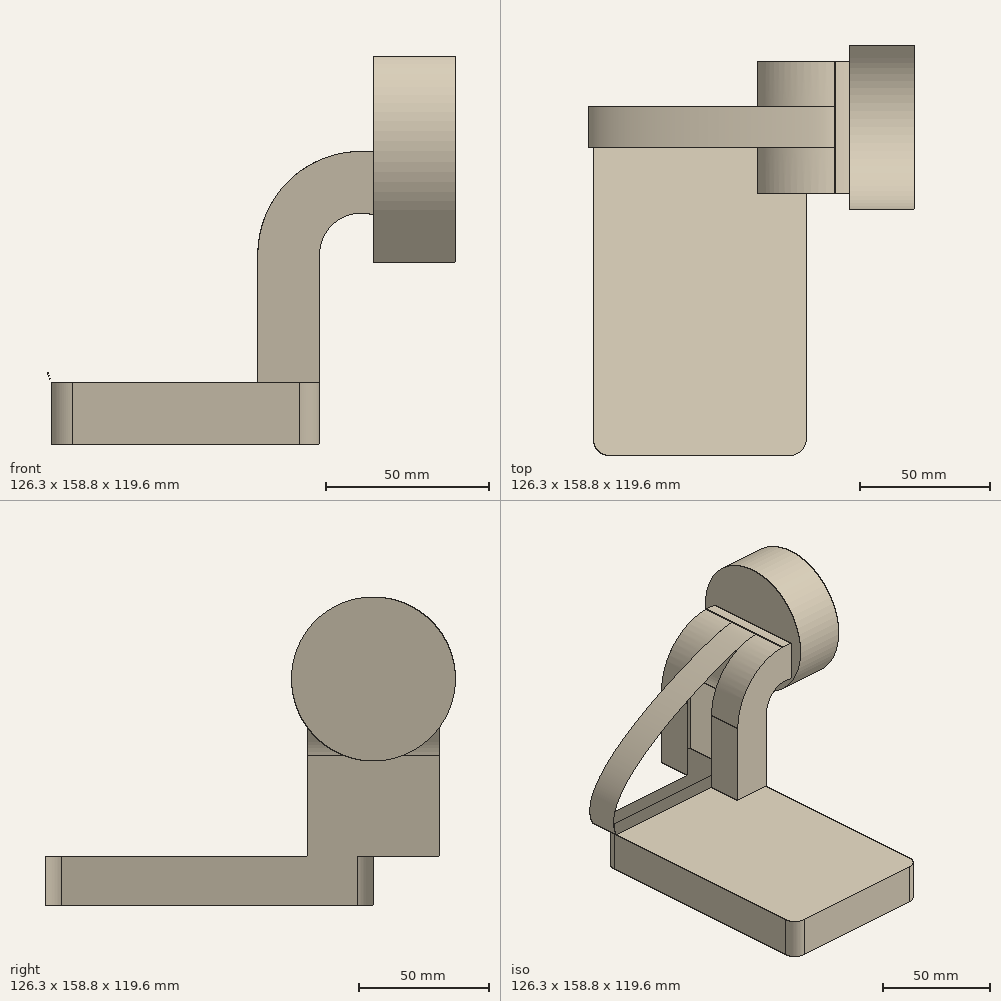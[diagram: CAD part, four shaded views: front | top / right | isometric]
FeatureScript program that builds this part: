
annotation { "Feature Type Name" : "Feature", "Feature Type Description" : "" }
export const myFeature = defineFeature(function(context is Context, id is Id, definition is map)
    precondition{}
    {
        {
            var Q0;
            Q0=qCreatedBy(makeId("Front.planeOp"),FACE);
            var sketch = newSketch(context, id + "F0", { "sketchPlane" : qUnion([Q0])});
            skLineSegment(sketch, "E0.bottom", {"start": v(-41.28, 9.52) * mm, "end": v(41.27, 9.53) * mm});
            skLineSegment(sketch, "E0.top", {"start": v(-41.28, -9.53) * mm, "end": v(41.28, -9.53) * mm});
            skLineSegment(sketch, "E0.left", {"start": v(-41.28, 9.52) * mm, "end": v(-41.28, -9.53) * mm});
            skLineSegment(sketch, "E0.right", {"start": v(41.27, 9.53) * mm, "end": v(41.28, -9.52) * mm});
            skPoint(sketch, "E0.middle", {"position": v(0, 0) * mm});
            skLineSegment(sketch, "E1.bottom", {"start": v(57.75, 46.59) * mm, "end": v(108.55, 46.59) * mm});
            skLineSegment(sketch, "E1.top", {"start": v(57.75, 78.34) * mm, "end": v(108.55, 78.34) * mm});
            skLineSegment(sketch, "E1.left", {"start": v(57.75, 46.59) * mm, "end": v(57.75, 78.34) * mm});
            skLineSegment(sketch, "E1.right", {"start": v(108.55, 46.59) * mm, "end": v(108.55, 78.34) * mm});
            skPoint(sketch, "E1.middle", {"position": v(83.15, 62.46) * mm});
            skLineSegment(sketch, "E2", {"start": v(41.27, 9.53) * mm, "end": v(41.27, 48.79) * mm});
            skArc(sketch, "E3", {"start": v(41.28, 48.79) * mm, "mid": v(49.51, 60.87) * mm, "end": v(63.77, 57.63) * mm});
            skLineSegment(sketch, "E4", {"start": v(63.77, 57.63) * mm, "end": v(75.18, 57.63) * mm});
            skLineSegment(sketch, "E5.0", {"start": v(70.02, 76.68) * mm, "end": v(75.18, 76.68) * mm});
            skArc(sketch, "E5.1", {"start": v(22.23, 48.79) * mm, "mid": v(38.11, 76.46) * mm, "end": v(70.02, 76.68) * mm});
            skLineSegment(sketch, "E5.2", {"start": v(22.22, 9.53) * mm, "end": v(22.22, 48.79) * mm});
            skLineSegment(sketch, "E6", {"start": v(83.15, 78.34) * mm, "end": v(83.15, 46.59) * mm});
            skFitSpline(sketch, "E7", {"points": [v(-41.28, 9.52) * mm, v(43.56, 78.98) * mm, v(52.4, 80.77) * mm], "startDerivative": vector(-57.77, 109.32) * mm, "endDerivative": vector(11.12, 1.28) * mm});
            skSolve(sketch);
        }
        {
            var Q0;
            Q0=makeQuery(id+"F0.imprint","IMPRINT",FACE,{"disambiguationData":[TD([[makeQuery(id+"F0.imprint","IMPRINT",EDGE,{"derivedFrom":sQuery(id+"F0.wireOp",EDGE,"E0.top")}),1.0]])]});
            extrude(context, id + "F1", {"entities" : qUnion([Q0]), "depth" : 127 * mm});
        }
        {
            var Q0;
            {var subQ0=sQuery(id+"F0.wireOp",EDGE,"E2");Q0=makeQuery(id+"F0.imprint","IMPRINT",FACE,{"disambiguationData":[TD([[makeQuery(id+"F0.imprint","IMPRINT",EDGE,{"derivedFrom":subQ0}),1.0]])]});}
            extrude(context, id + "F2", {"entities" : qUnion([Q0]), "operationType" : NewBodyOperationType.ADD, "endBound" : BoundingType.SYMMETRIC, "depth" : 50.8 * mm});
        }
        {
            var Q0;
            {var subQ3=sQuery(id+"F0.wireOp",EDGE,"E5.2");Q0=makeQuery(id+"F0.imprint","IMPRINT",FACE,{"disambiguationData":[TD([[makeQuery(id+"F0.imprint","IMPRINT",EDGE,{"derivedFrom":subQ3}),1.0]])]});}
            extrude(context, id + "F3", {"entities" : qUnion([Q0]), "operationType" : NewBodyOperationType.ADD, "endBound" : BoundingType.SYMMETRIC, "depth" : 15.88 * mm});
        }
        {
            var Q0;
            {var subQ4=sQuery(id+"F0.wireOp",EDGE,"E6");Q0=makeQuery(id+"F0.imprint","IMPRINT",FACE,{"disambiguationData":[TD([[makeQuery(id+"F0.imprint","IMPRINT",EDGE,{"derivedFrom":subQ4}),-1.0]])]});}
            var Q1;
            Q1=sQuery(id+"F0.wireOp",EDGE,"E1.top");
            revolve(context, id + "F4", {"operationType" : NewBodyOperationType.ADD, "entities" : qUnion([Q0]), "axis" : qUnion([Q1]), "revolveType" : RevolveType.FULL});
        }
        {
            var Q0;
            Q0=makeQuery(id+"F1.opExtrude","CAP_EDGE",EDGE,{"disambiguationData":[OSD([sQuery(id+"F0.wireOp",EDGE,"E0.right")])],"isStart":false});
            var Q1;
            Q1=makeQuery(id+"F1.opExtrude","CAP_EDGE",EDGE,{"disambiguationData":[OSD([sQuery(id+"F0.wireOp",EDGE,"E0.left")])],"isStart":false});
            var Q2;
            Q2=makeQuery(id+"F1.opExtrude","CAP_EDGE",EDGE,{"disambiguationData":[OSD([sQuery(id+"F0.wireOp",EDGE,"E0.right")])],"isStart":true});
            var Q3;
            Q3=makeQuery(id+"F1.opExtrude","CAP_EDGE",EDGE,{"disambiguationData":[OSD([sQuery(id+"F0.wireOp",EDGE,"E0.left")])],"isStart":true});
            fillet(context, id + "F5", {"entities" : qUnion([Q0, Q1, Q2, Q3]), "radius" : 6.35 * mm, "tangentPropagation" : true, "allowEdgeOverflow" : false});
        }
    });
